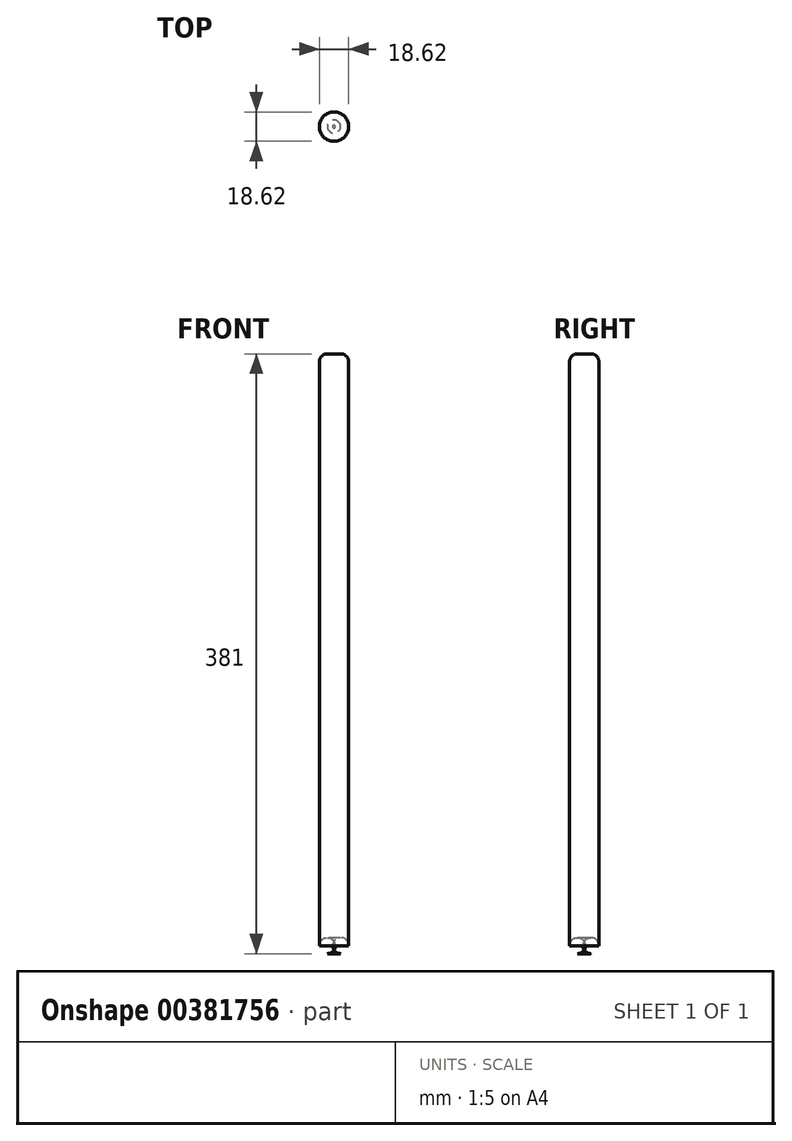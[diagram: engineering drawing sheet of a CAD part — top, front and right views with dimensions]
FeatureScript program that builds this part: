
annotation { "Feature Type Name" : "Feature", "Feature Type Description" : "" }
export const myFeature = defineFeature(function(context is Context, id is Id, definition is map)
    precondition{}
    {
        {
            var Q0;
            Q0=qCreatedBy(makeId("Top.planeOp"),FACE);
            var sketch = newSketch(context, id + "F0", { "sketchPlane" : qUnion([Q0])});
            skPoint(sketch, "E0", {"position": v(0, 0) * mm});
            skCircle(sketch, "E1", {"center": v(0, 0) * mm, "radius": 9.3 * mm});
            skSolve(sketch);
        }
        {
            var Q0;
            Q0=qSketchRegion(id+"F0",true);
            extrude(context, id + "F1", {"entities" : qUnion([Q0]), "depth" : 381 * mm});
        }
        {
            var Q0;
            Q0=makeQuery(id+"F1.opExtrude","CAP_EDGE",EDGE,{"disambiguationData":[OSD([sQuery(id+"F0.wireOp",EDGE,"E1")])],"isStart":true});
            fillet(context, id + "F2", {"entities" : qUnion([Q0]), "radius" : 5.08 * mm, "tangentPropagation" : true, "allowEdgeOverflow" : false});
        }
        {
            var Q0;
            Q0=makeQuery(id+"F1.opExtrude","CAP_EDGE",EDGE,{"disambiguationData":[OSD([sQuery(id+"F0.wireOp",EDGE,"E1")])],"isStart":false});
            fillet(context, id + "F3", {"entities" : qUnion([Q0]), "radius" : 5.08 * mm, "tangentPropagation" : true, "allowEdgeOverflow" : false});
        }
    });
